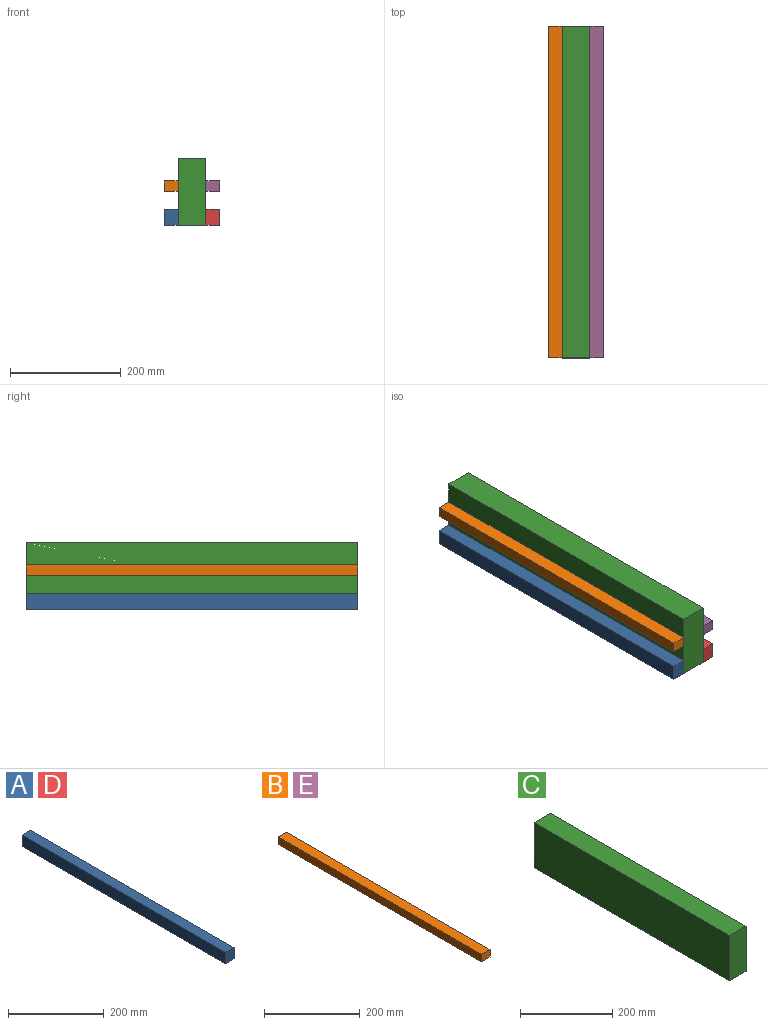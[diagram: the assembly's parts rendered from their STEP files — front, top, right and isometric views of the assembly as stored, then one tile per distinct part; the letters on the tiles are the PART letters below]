
ASSEMBLY  parts=5 mates=4
PART A: 6 faces, bbox 25x600x29 mm
  f0: plane 600x29mm, normal (1,0,0), area 17400mm2, adj f1,f3,f4,f5
  f1: plane 600x25mm, normal (0,0,1), area 15000mm2, adj f0,f2,f4,f5
  f2: plane 600x29mm, normal (-1,0,0), area 17400mm2, adj f1,f3,f4,f5
  f3: plane 600x25mm, normal (0,0,-1), area 15000mm2, adj f0,f2,f4,f5
  f4: plane 29x25mm, normal (0,-1,0), area 725mm2, adj f0,f1,f2,f3
  f5: plane 29x25mm, normal (0,1,0), area 725mm2, adj f0,f1,f2,f3
PART B: 6 faces, bbox 25x600x19 mm
  f0: plane 600x19mm, normal (1,0,0), area 11400mm2, adj f1,f3,f4,f5
  f1: plane 600x25mm, normal (0,0,1), area 15000mm2, adj f0,f2,f4,f5
  f2: plane 600x19mm, normal (-1,0,0), area 11400mm2, adj f1,f3,f4,f5
  f3: plane 600x25mm, normal (0,0,-1), area 15000mm2, adj f0,f2,f4,f5
  f4: plane 25x19mm, normal (0,-1,0), area 475mm2, adj f0,f1,f2,f3
  f5: plane 25x19mm, normal (0,1,0), area 475mm2, adj f0,f1,f2,f3
PART C: 6 faces, bbox 50x600x120 mm
  f0: plane 600x120mm, normal (1,0,0), area 72000mm2, adj f1,f3,f4,f5
  f1: plane 600x50mm, normal (0,0,1), area 30000mm2, adj f0,f2,f4,f5
  f2: plane 600x120mm, normal (-1,0,0), area 72000mm2, adj f1,f3,f4,f5
  f3: plane 600x50mm, normal (0,0,-1), area 30000mm2, adj f0,f2,f4,f5
  f4: plane 120x50mm, normal (0,-1,0), area 6000mm2, adj f0,f1,f2,f3
  f5: plane 120x50mm, normal (0,1,0), area 6000mm2, adj f0,f1,f2,f3
PART D: same geometry as A
PART E: same geometry as B
PLACE A t=(-74.97,-79.25,85.55)mm
PLACE B t=(2.64,-79.25,146.55)mm
PLACE C t=(215.94,-79.25,110.52)mm
PLACE D t=(0.03,-79.25,85.55)mm
PLACE E t=(77.64,-79.25,146.55)mm
MATE fastened E.f4 <-> C.f4  axis (0,-1,0) through (-559.21,-679.25,-42.94)mm
MATE fastened A.f4 <-> C.f4  axis (0,-1,0) through (-609.21,-679.25,-122.94)mm
MATE fastened B.f4 <-> C.f4  axis (0,-1,0) through (-609.21,-679.25,-42.94)mm
MATE fastened D.f4 <-> C.f4  axis (0,-1,0) through (-559.21,-679.25,-122.94)mm
